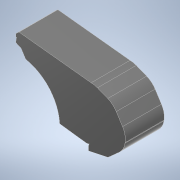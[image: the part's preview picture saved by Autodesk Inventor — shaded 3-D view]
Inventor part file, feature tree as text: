
AUTODESK INVENTOR PART (.ipt)
format: ipt  version: 2022 (Build 260153000, 153)  size: 344,576 bytes
history: native  units: in
note: dims shown in document units (in); Inventor stores cm internally (conversion verified against a paired STEP export)
features: extrude x2, sketch x2, other x1
ambient origin geometry x8: Origin, YZ Plane, XZ Plane, XY Plane, X Axis, Y Axis, Z Axis, Center Point
bodies: Body1 (feature_tree)
feature tree (5):
  other  "Sólido1"
  extrude  "Extrusión1"  Depth=0.2559in TaperAngle=0.0deg
  extrude  "Extrusión2"  Depth=0.0315in TaperAngle=0.0deg
  sketch  "Boceto1"  dims[d1=0.0787in d2=0.0394in d3=0.2559in d4=0.0in]
  sketch  "Boceto2"  dims[d7=0.1634in d8=0.4055in d9=0.1496in d10=0.0709in d11=0.4331in d12=0.2756in d13=0.0787in d14=0.0315in d15=0.0in]
